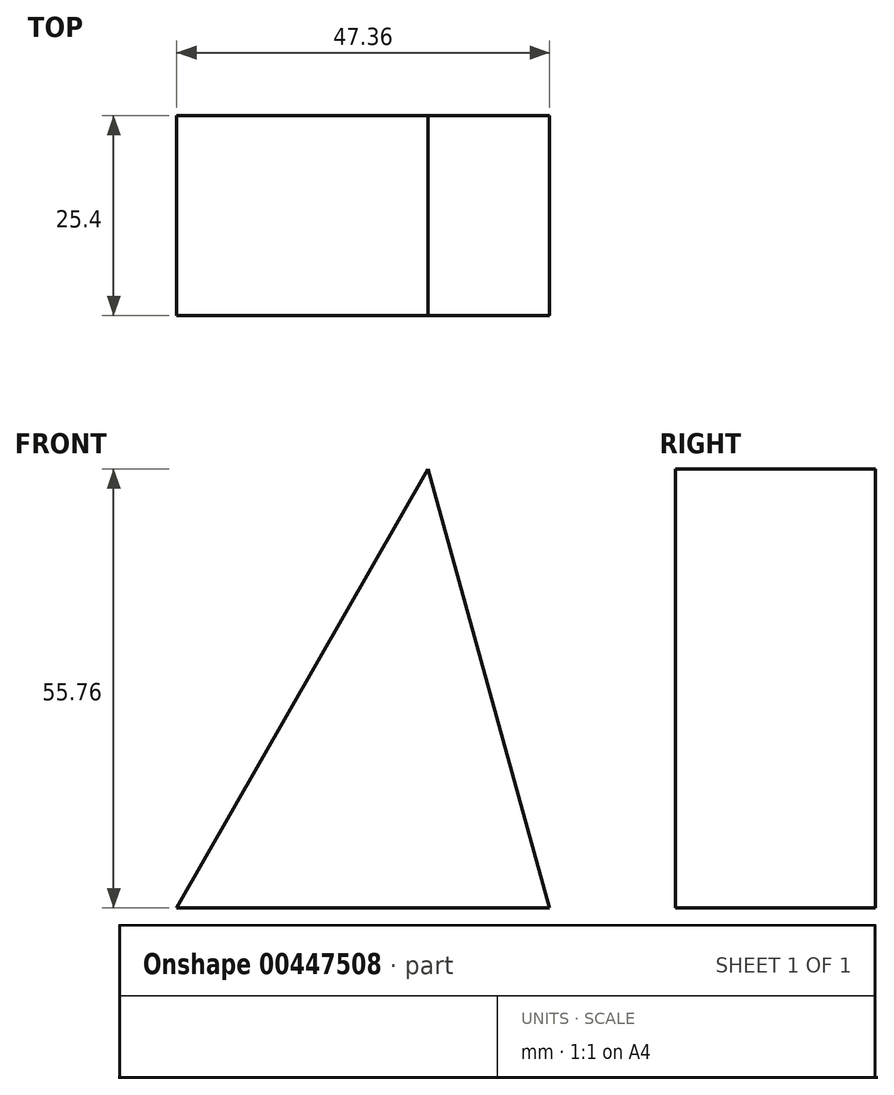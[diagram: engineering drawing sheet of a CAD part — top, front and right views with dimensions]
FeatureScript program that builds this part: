
annotation { "Feature Type Name" : "Feature", "Feature Type Description" : "" }
export const myFeature = defineFeature(function(context is Context, id is Id, definition is map)
    precondition{}
    {
        {
            var Q0;
            Q0=qCreatedBy(makeId("Front.planeOp"),FACE);
            var sketch = newSketch(context, id + "F0", { "sketchPlane" : qUnion([Q0])});
            skLineSegment(sketch, "E0", {"start": v(15.45, 0) * mm, "end": v(0, 55.76) * mm});
            skLineSegment(sketch, "E1", {"start": v(0, 55.76) * mm, "end": v(-31.91, 0) * mm});
            skLineSegment(sketch, "E2", {"start": v(-31.91, 0) * mm, "end": v(15.45, 0) * mm});
            skLineSegment(sketch, "E3", {"start": v(84.53, 44.8) * mm, "end": v(99.93, 65.56) * mm});
            skSolve(sketch);
        }
        {
            var Q0;
            Q0=makeQuery(id+"F0.imprint","IMPRINT",FACE,{"disambiguationData":[TD([[makeQuery(id+"F0.imprint","IMPRINT",EDGE,{"derivedFrom":sQuery(id+"F0.wireOp",EDGE,"E0")}),1.0]])]});
            extrude(context, id + "F1", {"entities" : qUnion([Q0]), "depth" : 25.4 * mm});
        }
    });
